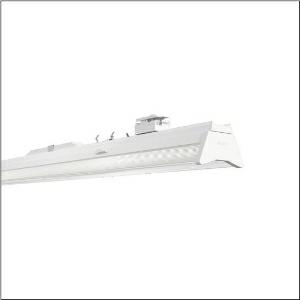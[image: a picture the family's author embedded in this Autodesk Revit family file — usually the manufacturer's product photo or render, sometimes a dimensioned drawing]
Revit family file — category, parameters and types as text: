
# Revit family: licross_r__21_performance_mo_52tm16cn46xg_6fd6
name_source: partatom
category: Lighting Fixtures
units: mm (PartAtom-declared; Revit-internal decimal feet)

## family parameters
Cut with Voids When Loaded = No
Host = Face
Light Source = No
Part Type = Normal
Room Calculation Point = No
Round Connector Dimension = Use Diameter
Shared = No

## types (1)
- --- (1 x LED, 6000 lm, 32 W, 4000K)
    Apparent Load = 32 VA
    CIE Flux Codes = 66 88 96 79 100
    Color Rendering = 80
    Color Temperature = 4000K
    Default Elevation = 1800 mm
    Description = Licross® 21 Performance MO, luminaire insert, of sheet steel, galvanised, coil coated, white, length: 1.500mm, width: 120mm, height: 123mm, LED rated luminous flux: 6.000lm, light colour: 840, control gear: ON/OFF Multilumen, CLOi, control gear: ECG Multilumen, with plug, 3-pole, with phase selection, mains connection: 220..240V, AC, 50/60Hz, halogen-free wiring, primary light control with lens, of plastic, primary optical cover: cover, of PMMA, light emission: direct/indirect distribution, primary light characteristic: symmetric, protection rating (complete): IP40, insulation class (complete): insulation class I (protective earthing), certification: CE, ENEC, UKCA, protection symbol: D if used in an environment without relevant dust loads with corresponding accessories, impact resistance: IK06, permissible ambient temperature for indoor applications: -35..+55°C, corresponds to IFS (International Featured Standards) requirements for safety and quality in the food industry, reducing of maximum allowable ambient temperature of 5°C with ceiling mounting, LABS conformity tested according to VDMA 24364:2018-05, packaging unit: 1 piece
    Height = 114 mm
    Lamp = 1 x LED
    Lamp Light Flux = 6000 lm
    Lamp Power = 32 W
    Lamp count = 1
    Length = 1500 mm
    Luminous efficacy = 188 lm/W
    Manufacturer = Siteco
    ModVariant = No
    Model = 52TM16CN46XG
    Mounting Place = Ceiling
    Mounting Type = Pendant
    Number of Poles = 1
    OnlyDefault = Yes
    Power Factor = 1
    Product Name = Licross® 21 Performance MO
    Product group = luminaire insert
    ProductGroupID = 902
    Protection Class = Protection class I
    Protection Degree = IP 40
    RLX_Detail_Level = 1
    RlxData = <blob elided: 31805 chars, md5=20d4f465>
    Socket = socket
    Standby Power = 0 W
    System Light Flux = 6000 lm
    System Power = 32 W
    Type Comments = factory setting: luminous flux: 100 % | (A | C | E) | 74 mA
    Type Image = l_1256138.jpg
    URL = http://relux.com
    VarID = @adj_020001
    Voltage = 0 V
    Weight = 0.00 kg
    Width = 120 mm

## geometry (parser evidence)
native form markers: Blend x4, Sweep x11
no freeform markers — native parametric forms only
